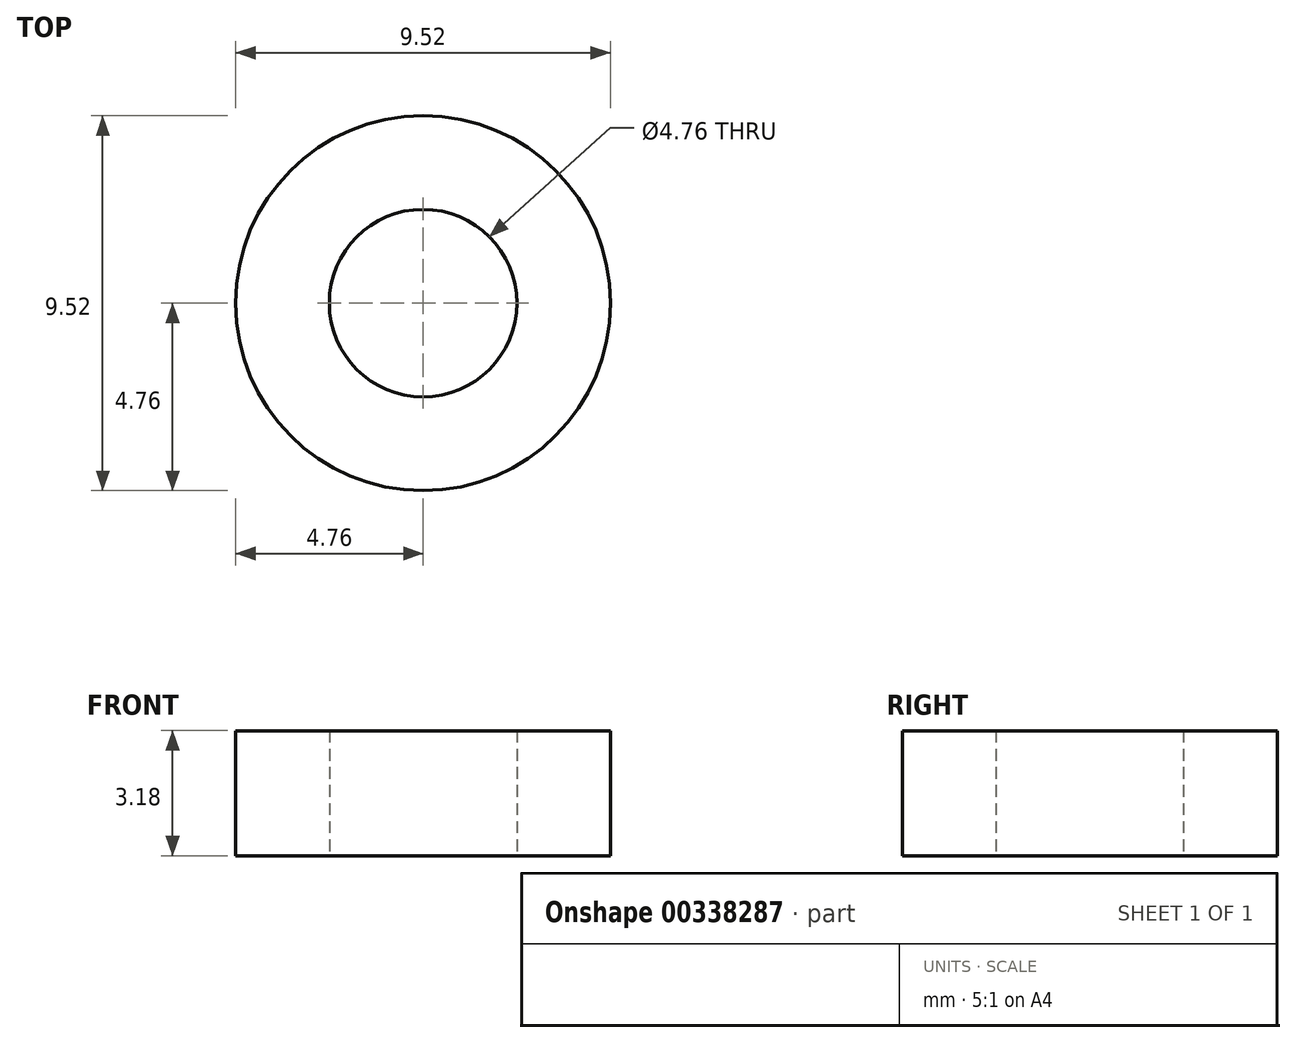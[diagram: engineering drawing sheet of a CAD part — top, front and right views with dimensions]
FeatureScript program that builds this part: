
annotation { "Feature Type Name" : "Feature", "Feature Type Description" : "" }
export const myFeature = defineFeature(function(context is Context, id is Id, definition is map)
    precondition{}
    {
        {
            var Q0;
            Q0=qCreatedBy(makeId("Top.planeOp"),FACE);
            var sketch = newSketch(context, id + "F0", { "sketchPlane" : qUnion([Q0])});
            skCircle(sketch, "E0", {"center": v(0, 0) * mm, "radius": 2.38 * mm});
            skCircle(sketch, "E1", {"center": v(0, 0) * mm, "radius": 4.76 * mm});
            skSolve(sketch);
        }
        {
            var Q0;
            Q0 = qSketchRegion(id + "F0", true);
            extrude(context, id + "F1", {"entities" : qUnion([Q0]), "depth" : 3.17 * mm});
        }
    });
